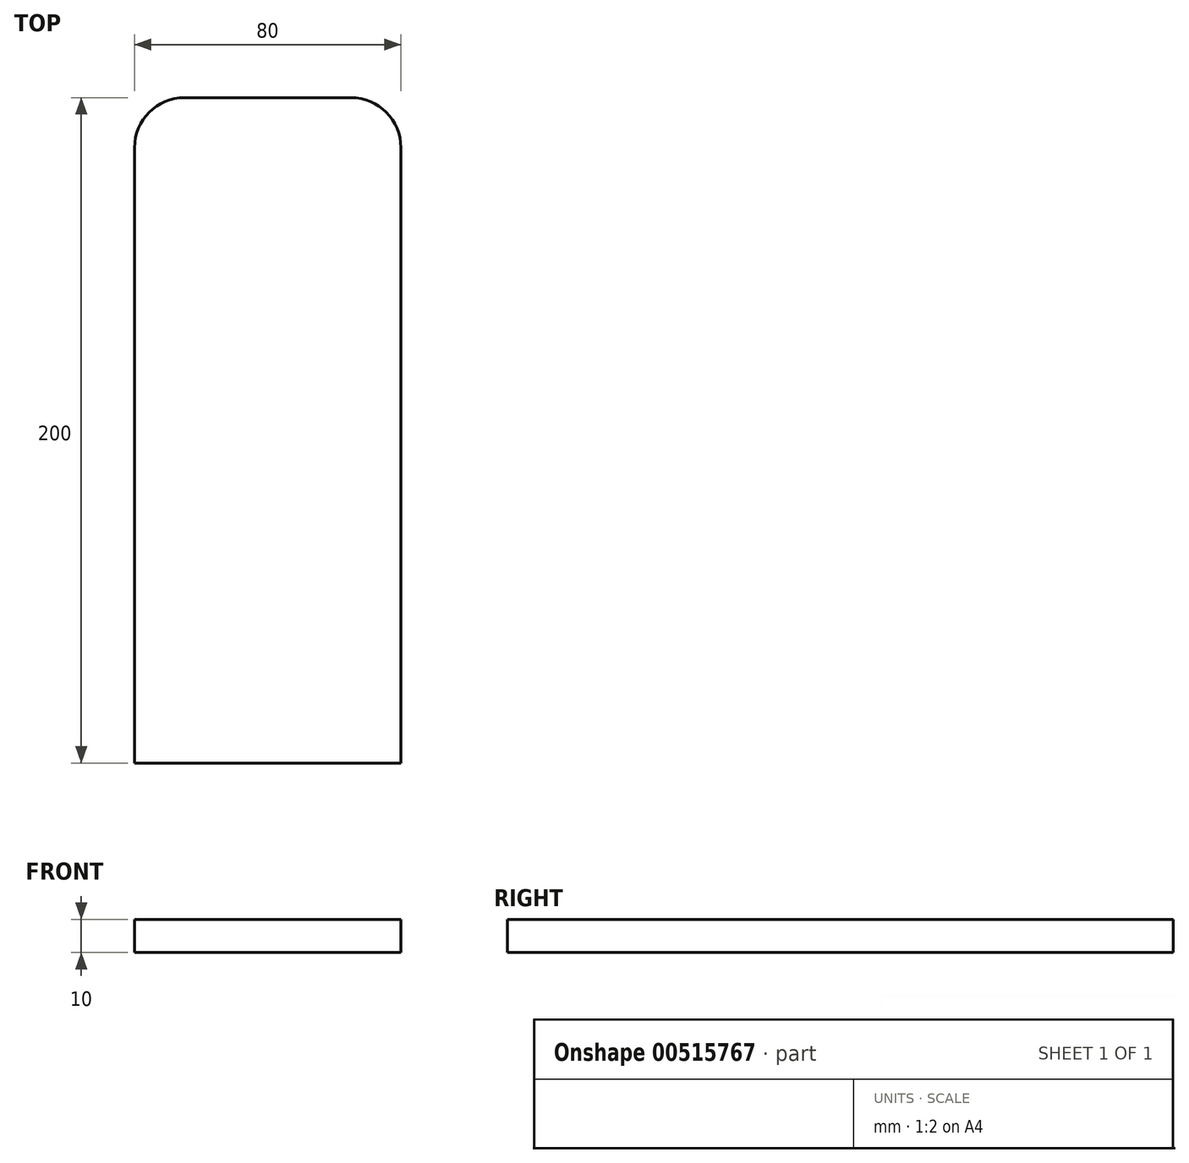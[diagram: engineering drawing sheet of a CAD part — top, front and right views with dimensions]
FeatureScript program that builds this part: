
annotation { "Feature Type Name" : "Feature", "Feature Type Description" : "" }
export const myFeature = defineFeature(function(context is Context, id is Id, definition is map)
    precondition{}
    {
        {
            var Q0;
            Q0=qCreatedBy(makeId("Top.planeOp"),FACE);
            var sketch = newSketch(context, id + "F0", { "sketchPlane" : qUnion([Q0])});
            skLineSegment(sketch, "E0", {"start": v(0, 29.64) * mm, "end": v(11.02, 29.64) * mm});
            skFitSpline(sketch, "E1", {"points": [v(11.02, 29.64) * mm, v(29.42, 24.58) * mm, v(34.62, 8.57) * mm], "startDerivative": vector(50.85, 0) * mm, "endDerivative": vector(0.87, -44.99) * mm});
            skLineSegment(sketch, "E2.MirrorCS", {"start": v(0, 29.64) * mm, "end": v(-11.02, 29.64) * mm});
            skFitSpline(sketch, "E3.MirrorCS", {"points": [v(-11.02, 29.64) * mm, v(-29.42, 24.58) * mm, v(-34.62, 8.57) * mm], "startDerivative": vector(-50.85, 0) * mm, "endDerivative": vector(-0.87, -44.99) * mm});
            skLineSegment(sketch, "E4", {"start": v(34.62, 8.57) * mm, "end": v(34.62, -34.96) * mm});
            skLineSegment(sketch, "E5", {"start": v(0, -34.96) * mm, "end": v(34.62, -34.96) * mm});
            skLineSegment(sketch, "E6.MirrorCS", {"start": v(-34.62, 8.57) * mm, "end": v(-34.62, -34.96) * mm});
            skLineSegment(sketch, "E7.MirrorCS", {"start": v(0, -34.96) * mm, "end": v(-34.62, -34.96) * mm});
            skPoint(sketch, "E8.orphan", {"position": v(0, 0) * mm});
            skSolve(sketch);
        }
        {
            var Q0;
            Q0=makeQuery(id+"F0.imprint","IMPRINT",FACE,{"disambiguationData":[TD([[makeQuery(id+"F0.imprint","IMPRINT",EDGE,{"derivedFrom":sQuery(id+"F0.wireOp",EDGE,"E0")}),-1.0]])]});
            extrude(context, id + "F1", {"entities" : qUnion([Q0]), "depth" : 2.54 * mm, "offsetDistance" : 25.4 * mm});
        }
        {
            var Q0;
            Q0=makeQuery(id+"F1.opExtrude","SWEPT_BODY",BODY,{"disambiguationData":[OSD([sQuery(id+"F0.wireOp",EDGE,"E0"),sQuery(id+"F0.wireOp",EDGE,"E1"),sQuery(id+"F0.wireOp",EDGE,"E2.MirrorCS"),sQuery(id+"F0.wireOp",EDGE,"E3.MirrorCS"),sQuery(id+"F0.wireOp",EDGE,"E4"),sQuery(id+"F0.wireOp",EDGE,"E5"),sQuery(id+"F0.wireOp",EDGE,"E6.MirrorCS"),sQuery(id+"F0.wireOp",EDGE,"E7.MirrorCS")])]});
            deleteBodies(context, id + "F2", {"entities" : qUnion([Q0])});
        }
        {
            var Q0;
            Q0=qCreatedBy(makeId("Top.planeOp"),FACE);
            var sketch = newSketch(context, id + "F3", { "sketchPlane" : qUnion([Q0])});
            skLineSegment(sketch, "E9.bottom", {"start": v(0, 0) * mm, "end": v(80, 0) * mm});
            skLineSegment(sketch, "E9.top", {"start": v(15, 200) * mm, "end": v(65, 200) * mm});
            skLineSegment(sketch, "E9.left", {"start": v(0, 0) * mm, "end": v(0, 185) * mm});
            skLineSegment(sketch, "E9.right", {"start": v(80, 0) * mm, "end": v(80, 185) * mm});
            skArc(sketch, "E10", {"start": v(15, 200) * mm, "mid": v(4.4, 195.6) * mm, "end": v(0, 185) * mm});
            skArc(sketch, "E11", {"start": v(80, 185) * mm, "mid": v(75.6, 195.6) * mm, "end": v(65, 200) * mm});
            skSolve(sketch);
        }
        {
            var Q0;
            Q0 = qSketchRegion(id + "F3", true);
            extrude(context, id + "F4", {"entities" : qUnion([Q0]), "depth" : 10 * mm, "offsetDistance" : 25 * mm});
        }
    });
